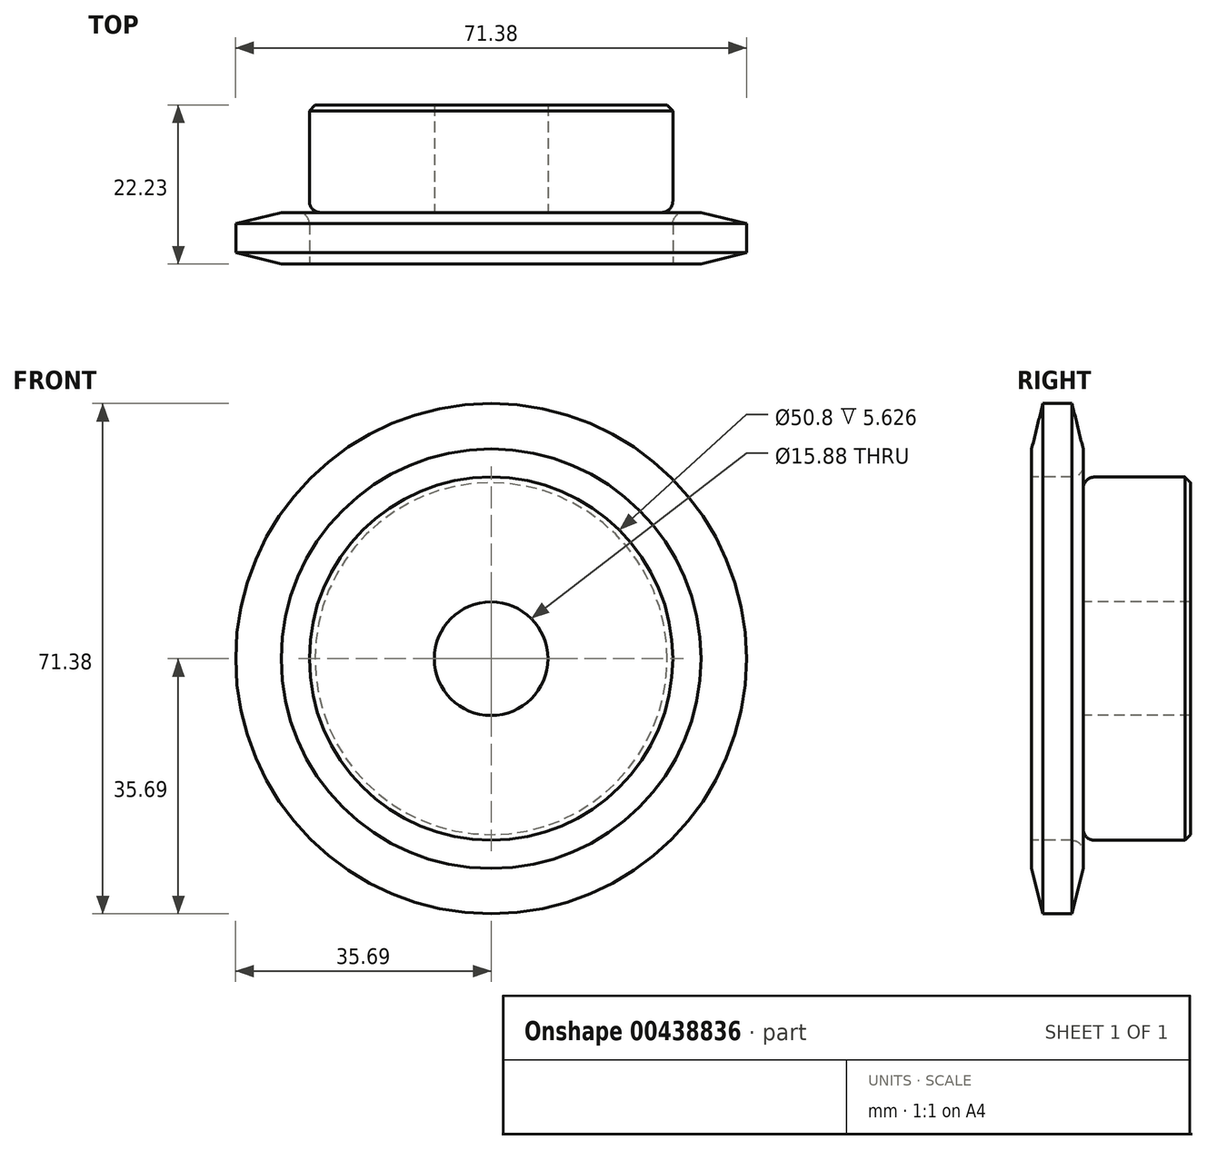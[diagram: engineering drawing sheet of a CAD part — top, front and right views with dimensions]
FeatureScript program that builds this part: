
annotation { "Feature Type Name" : "Feature", "Feature Type Description" : "" }
export const myFeature = defineFeature(function(context is Context, id is Id, definition is map)
    precondition{}
    {
        {
            var Q0;
            Q0=qCreatedBy(makeId("Right.planeOp"),FACE);
            var sketch = newSketch(context, id + "F0", { "sketchPlane" : qUnion([Q0])});
            skLineSegment(sketch, "E0", {"start": v(0, 0) * mm, "end": v(36.02, 0) * mm, "construction": true});
            skLineSegment(sketch, "E1.bottom", {"start": v(0, 35.69) * mm, "end": v(7.21, 35.69) * mm});
            skLineSegment(sketch, "E1.top", {"start": v(0, 7.94) * mm, "end": v(7.21, 7.94) * mm});
            skLineSegment(sketch, "E1.left", {"start": v(0, 35.69) * mm, "end": v(0, 7.94) * mm});
            skLineSegment(sketch, "E1.right", {"start": v(7.21, 35.69) * mm, "end": v(7.21, 7.94) * mm});
            skLineSegment(sketch, "E2.bottom", {"start": v(0, 25.4) * mm, "end": v(22.23, 25.4) * mm});
            skLineSegment(sketch, "E2.top", {"start": v(0, 7.94) * mm, "end": v(22.22, 7.94) * mm});
            skLineSegment(sketch, "E2.left", {"start": v(0, 25.4) * mm, "end": v(0, 7.94) * mm});
            skLineSegment(sketch, "E2.right", {"start": v(22.23, 25.4) * mm, "end": v(22.23, 7.94) * mm});
            skLineSegment(sketch, "E3.MirrorCS", {"start": v(0, -7.94) * mm, "end": v(22.22, -7.94) * mm});
            skLineSegment(sketch, "E4.MirrorCS", {"start": v(7.21, -35.69) * mm, "end": v(7.21, -7.94) * mm});
            skLineSegment(sketch, "E5.MirrorCS", {"start": v(0, -25.4) * mm, "end": v(0, -7.94) * mm});
            skLineSegment(sketch, "E6.MirrorCS", {"start": v(0, -35.69) * mm, "end": v(7.21, -35.69) * mm});
            skLineSegment(sketch, "E7.MirrorCS", {"start": v(22.23, -25.4) * mm, "end": v(22.22, -7.94) * mm});
            skLineSegment(sketch, "E8.MirrorCS", {"start": v(0, -35.69) * mm, "end": v(0, -7.94) * mm});
            skLineSegment(sketch, "E9.MirrorCS", {"start": v(0, -25.4) * mm, "end": v(22.23, -25.4) * mm});
            skSolve(sketch);
        }
        {
            var Q0;
            {var subQ5=sQuery(id+"F0.wireOp",EDGE,"E2.right");Q0=makeQuery(id+"F0.imprint","IMPRINT",FACE,{"disambiguationData":[TD([[makeQuery(id+"F0.imprint","IMPRINT",EDGE,{"derivedFrom":subQ5}),-1.0]])]});}
            var Q1;
            {var subQ5=sQuery(id+"F0.wireOp",EDGE,"E2.left");Q1=makeQuery(id+"F0.imprint","IMPRINT",FACE,{"disambiguationData":[TD([[makeQuery(id+"F0.imprint","IMPRINT",EDGE,{"derivedFrom":subQ5}),1.0]])]});}
            var Q2;
            {var subQ0=sQuery(id+"F0.wireOp",EDGE,"E1.bottom");Q2=makeQuery(id+"F0.imprint","IMPRINT",FACE,{"disambiguationData":[TD([[makeQuery(id+"F0.imprint","IMPRINT",EDGE,{"derivedFrom":subQ0}),-1.0]])]});}
            var Q3;
            Q3=sQuery(id+"F0.wireOp",EDGE,"E0");
            revolve(context, id + "F1", {"entities" : qUnion([Q0, Q1, Q2]), "axis" : qUnion([Q3]), "revolveType" : RevolveType.FULL});
        }
        {
            var Q0;
            Q0=makeQuery(id+"F1.opRevolve","SWEPT_EDGE",EDGE,{"disambiguationData":[OSD([sQuery(id+"F0.wireOp",EDGE,"E1.right"),sQuery(id+"F0.wireOp",EDGE,"E2.bottom")])]});
            fillet(context, id + "F2", {"entities" : qUnion([Q0]), "radius" : 1.59 * mm, "tangentPropagation" : true, "allowEdgeOverflow" : false});
        }
        {
            var Q0;
            Q0=makeQuery(id+"F1.opRevolve","SWEPT_EDGE",EDGE,{"disambiguationData":[OSD([sQuery(id+"F0.wireOp",EDGE,"E2.bottom"),sQuery(id+"F0.wireOp",EDGE,"E2.right")])]});
            chamfer(context, id + "F3", {"entities" : qUnion([Q0]), "width" : 0.8 * mm, "tangentPropagation" : true});
        }
        {
            var Q0;
            Q0=makeQuery(id+"F1.opRevolve","SWEPT_EDGE",EDGE,{"disambiguationData":[OSD([sQuery(id+"F0.wireOp",EDGE,"E1.bottom"),sQuery(id+"F0.wireOp",EDGE,"E1.left")])]});
            var Q1;
            Q1=makeQuery(id+"F1.opRevolve","SWEPT_EDGE",EDGE,{"disambiguationData":[OSD([sQuery(id+"F0.wireOp",EDGE,"E1.bottom"),sQuery(id+"F0.wireOp",EDGE,"E1.right")])]});
            chamfer(context, id + "F4", {"entities" : qUnion([Q0, Q1]), "chamferType" : ChamferType.TWO_OFFSETS, "width1" : 6.35 * mm, "oppositeDirection" : false, "width2" : 1.57 * mm, "tangentPropagation" : true});
        }
    });
